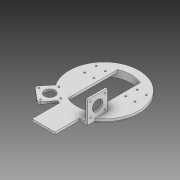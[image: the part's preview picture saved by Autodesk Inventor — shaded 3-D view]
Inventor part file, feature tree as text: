
AUTODESK INVENTOR PART (.ipt)
format: ipt  version: 2020 (Build 240168000, 168)  size: 272,896 bytes
history: native  units: mm
features: extrude x8, sketch x8, revolve x1, plane x1
ambient origin geometry x8: Origin, YZ Plane, XZ Plane, XY Plane, X Axis, Y Axis, Z Axis, Center Point
bodies: Solid1 (feature_tree)
feature tree (18):
  revolve  "Revolution1"  [1 undecoded]
  extrude  "Extrusion1"  Depth=3.0mm
  extrude  "Extrusion2"  TaperAngle=90.0deg  [1 undecoded]
  extrude  "Extrusion3"  Depth=5.0mm
  sketch  "Sketch5"  dims[d8=76.0mm d9=49.5mm]
  extrude  "Extrusion4"  Depth=49.5mm
  extrude  "Extrusion5"  Depth=5.0mm
  extrude  "Extrusion6"  Depth=25.0mm
  plane  "Work Plane1"
  extrude  "Extrusion7"  Depth=4.0mm
  extrude  "Extrusion8"  TaperAngle=0.0deg  [1 undecoded]
  sketch  "Sketch1"  dims[d0=63.4mm d1=4.0mm]
  sketch  "Sketch2"  dims[d2=2.5mm d3=3.0mm]
  sketch  "Sketch3"  dims[d4=5.0mm d5=90.0deg]
  sketch  "Sketch4"  dims[d6=6.0mm d7=5.0mm]
  sketch  "Sketch6"  dims[d10=5.0mm d11=0.0mm d12=25.0mm]
  sketch  "Sketch7"  dims[d14=20.0mm d15=25.0mm]
  sketch  "Sketch8"  dims[d16=20.0mm d17=3.5mm d18=0.0mm d19=0.0mm d20=60.0mm d21=50.0mm d22=5.0mm d23=0.0mm d24=20.6mm d25=31.0mm d26=42.0mm d27=10.0mm d28=0.0mm d29=3.5mm d30=23.0mm d31=6.981317mm d32=0.0mm d33=0.0mm d34=6.0mm d35=3.0mm d36=0.0mm d37=5.0mm d38=84.0mm d39=-14.0mm d40=84.0mm d41=23.0mm d42=3.5mm d43=31.0mm d44=31.0mm d46=40.0mm d47=43.0mm d48=4.0mm d49=0.0mm d50=4.0mm d51=0.0mm]
note: 3 required parameter values undecoded (feature->parameter linkage not recoverable at this tier; creation-order binding heuristic only, values carry confidence <= 0.55)